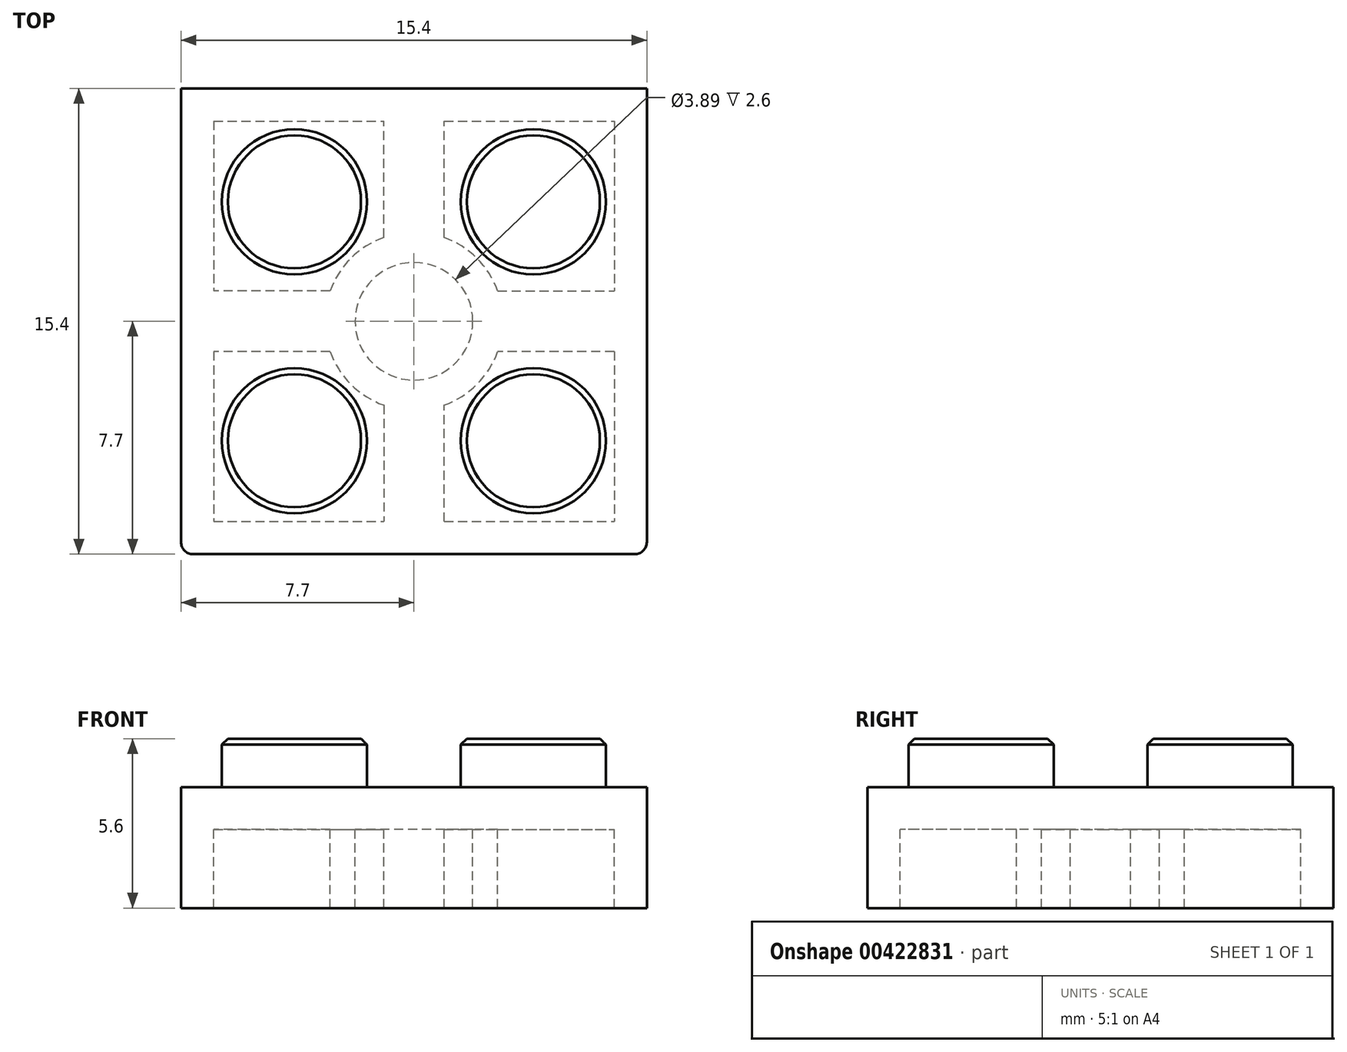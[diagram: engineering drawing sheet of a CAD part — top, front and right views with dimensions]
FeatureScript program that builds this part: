
annotation { "Feature Type Name" : "Feature", "Feature Type Description" : "" }
export const myFeature = defineFeature(function(context is Context, id is Id, definition is map)
    precondition{}
    {
        {
            var Q0;
            Q0=qCreatedBy(makeId("Top.planeOp"),FACE);
            var sketch = newSketch(context, id + "F0", { "sketchPlane" : qUnion([Q0])});
            skLineSegment(sketch, "E0.bottom", {"start": v(-7.7, 7.7) * mm, "end": v(7.7, 7.7) * mm});
            skLineSegment(sketch, "E0.top", {"start": v(-7.7, -7.7) * mm, "end": v(7.7, -7.7) * mm});
            skLineSegment(sketch, "E0.left", {"start": v(-7.7, 7.7) * mm, "end": v(-7.7, -7.7) * mm});
            skLineSegment(sketch, "E0.right", {"start": v(7.7, 7.7) * mm, "end": v(7.7, -7.7) * mm});
            skLineSegment(sketch, "E1", {"start": v(-7.7, 7.7) * mm, "end": v(7.7, -7.7) * mm, "construction": true});
            skLineSegment(sketch, "E2", {"start": v(7.7, 7.7) * mm, "end": v(-7.7, -7.7) * mm, "construction": true});
            skLineSegment(sketch, "E3.bottom", {"start": v(-3.95, 3.95) * mm, "end": v(3.95, 3.95) * mm, "construction": true});
            skLineSegment(sketch, "E3.top", {"start": v(-3.95, -3.95) * mm, "end": v(3.95, -3.95) * mm, "construction": true});
            skLineSegment(sketch, "E3.left", {"start": v(-3.95, 3.95) * mm, "end": v(-3.95, -3.95) * mm, "construction": true});
            skLineSegment(sketch, "E3.right", {"start": v(3.95, 3.95) * mm, "end": v(3.95, -3.95) * mm, "construction": true});
            skCircle(sketch, "E4", {"center": v(3.95, 3.95) * mm, "radius": 2.4 * mm});
            skCircle(sketch, "E5", {"center": v(-3.95, 3.95) * mm, "radius": 2.4 * mm});
            skCircle(sketch, "E6", {"center": v(-3.95, -3.95) * mm, "radius": 2.4 * mm});
            skCircle(sketch, "E7", {"center": v(3.95, -3.95) * mm, "radius": 2.4 * mm});
            skLineSegment(sketch, "E8.bottom", {"start": v(-6.35, 6.35) * mm, "end": v(6.35, 6.35) * mm});
            skLineSegment(sketch, "E8.top", {"start": v(-6.35, -6.35) * mm, "end": v(6.35, -6.35) * mm});
            skLineSegment(sketch, "E8.left", {"start": v(-6.35, 6.35) * mm, "end": v(-6.35, -6.35) * mm});
            skLineSegment(sketch, "E8.right", {"start": v(6.35, 6.35) * mm, "end": v(6.35, -6.35) * mm});
            skCircle(sketch, "E9", {"center": v(0, 0) * mm, "radius": 2.95 * mm});
            skCircle(sketch, "E10", {"center": v(0, 0) * mm, "radius": 1.95 * mm});
            skLineSegment(sketch, "E11.bottom", {"start": v(-6.62, 6.62) * mm, "end": v(6.62, 6.62) * mm});
            skLineSegment(sketch, "E11.top", {"start": v(-6.62, -6.62) * mm, "end": v(6.62, -6.62) * mm});
            skLineSegment(sketch, "E11.left", {"start": v(-6.62, 6.62) * mm, "end": v(-6.62, -6.62) * mm});
            skLineSegment(sketch, "E11.right", {"start": v(6.62, 6.62) * mm, "end": v(6.62, -6.62) * mm});
            skPoint(sketch, "E12.center.orphan", {"position": v(0, 7.7) * mm});
            skPoint(sketch, "E13.center.orphan", {"position": v(0, 11.7) * mm});
            skSolve(sketch);
        }
        {
            var Q0;
            Q0=makeQuery(id+"F0.imprint","IMPRINT",FACE,{"disambiguationData":[TD([[makeQuery(id+"F0.imprint","IMPRINT",EDGE,{"derivedFrom":sQuery(id+"F0.wireOp",EDGE,"E0.bottom")}),1.0]])]});
            var Q1;
            Q1=makeQuery(id+"F0.imprint","IMPRINT",FACE,{"disambiguationData":[TD([[makeQuery(id+"F0.imprint","IMPRINT",EDGE,{"derivedFrom":sQuery(id+"F0.wireOp",EDGE,"E4")}),1.0]])]});
            var Q2;
            Q2=makeQuery(id+"F0.imprint","IMPRINT",FACE,{"disambiguationData":[TD([[makeQuery(id+"F0.imprint","IMPRINT",EDGE,{"derivedFrom":sQuery(id+"F0.wireOp",EDGE,"E5")}),1.0]])]});
            var Q3;
            Q3=makeQuery(id+"F0.imprint","IMPRINT",FACE,{"disambiguationData":[TD([[makeQuery(id+"F0.imprint","IMPRINT",EDGE,{"derivedFrom":sQuery(id+"F0.wireOp",EDGE,"E6")}),1.0]])]});
            var Q4;
            Q4=makeQuery(id+"F0.imprint","IMPRINT",FACE,{"disambiguationData":[TD([[makeQuery(id+"F0.imprint","IMPRINT",EDGE,{"derivedFrom":sQuery(id+"F0.wireOp",EDGE,"E7")}),1.0]])]});
            var Q5;
            Q5=makeQuery(id+"F0.imprint","IMPRINT",FACE,{"disambiguationData":[TD([[makeQuery(id+"F0.imprint","IMPRINT",EDGE,{"derivedFrom":sQuery(id+"F0.wireOp",EDGE,"E0.bottom")}),-1.0]])]});
            var Q6;
            {var subQ5=sQuery(id+"F0.wireOp",EDGE,"E8.bottom");var subQ13=sQuery(id+"F0.wireOp",EDGE,"E4");var subQ14=makeQuery(id+"F0.imprint","INTERSECT",VERTEX,{"derivedFrom":[subQ13,subQ5]});Q6=makeQuery(id+"F0.imprint","IMPRINT",FACE,{"disambiguationData":[TD([[makeQuery(id+"F0.imprint","IMPRINT",EDGE,{"disambiguationData":[TD([[subQ14,-1.0]])],"derivedFrom":subQ13}),-1.0]])]});}
            var Q7;
            {var subQ0=sQuery(id+"F0.wireOp",EDGE,"E8.top");var subQ1=sQuery(id+"F0.wireOp",EDGE,"E6");var subQ2=makeQuery(id+"F0.imprint","INTERSECT",VERTEX,{"derivedFrom":[subQ1,subQ0]});Q7=makeQuery(id+"F0.imprint","IMPRINT",FACE,{"disambiguationData":[TD([[makeQuery(id+"F0.imprint","IMPRINT",EDGE,{"disambiguationData":[TD([[subQ2,1.0]])],"derivedFrom":subQ1}),-1.0]])]});}
            var Q8;
            {var subQ0=sQuery(id+"F0.wireOp",EDGE,"E8.bottom");var subQ1=sQuery(id+"F0.wireOp",EDGE,"E5");var subQ2=makeQuery(id+"F0.imprint","INTERSECT",VERTEX,{"derivedFrom":[subQ1,subQ0]});Q8=makeQuery(id+"F0.imprint","IMPRINT",FACE,{"disambiguationData":[TD([[makeQuery(id+"F0.imprint","IMPRINT",EDGE,{"disambiguationData":[TD([[subQ2,-1.0]])],"derivedFrom":subQ1}),-1.0]])]});}
            var Q9;
            {var subQ0=sQuery(id+"F0.wireOp",EDGE,"E8.bottom");var subQ1=sQuery(id+"F0.wireOp",EDGE,"E4");var subQ2=makeQuery(id+"F0.imprint","INTERSECT",VERTEX,{"derivedFrom":[subQ1,subQ0]});Q9=makeQuery(id+"F0.imprint","IMPRINT",FACE,{"disambiguationData":[TD([[makeQuery(id+"F0.imprint","IMPRINT",EDGE,{"disambiguationData":[TD([[subQ2,1.0]])],"derivedFrom":subQ1}),-1.0]])]});}
            var Q10;
            {var subQ0=sQuery(id+"F0.wireOp",EDGE,"E8.top");var subQ1=sQuery(id+"F0.wireOp",EDGE,"E7");var subQ2=makeQuery(id+"F0.imprint","INTERSECT",VERTEX,{"derivedFrom":[subQ1,subQ0]});Q10=makeQuery(id+"F0.imprint","IMPRINT",FACE,{"disambiguationData":[TD([[makeQuery(id+"F0.imprint","IMPRINT",EDGE,{"disambiguationData":[TD([[subQ2,-1.0]])],"derivedFrom":subQ1}),-1.0]])]});}
            var Q11;
            {var subQ0=sQuery(id+"F0.wireOp",EDGE,"E8.left");var subQ1=sQuery(id+"F0.wireOp",EDGE,"E5");var subQ2=makeQuery(id+"F0.imprint","INTERSECT",VERTEX,{"derivedFrom":[subQ1,subQ0]});Q11=makeQuery(id+"F0.imprint","IMPRINT",FACE,{"disambiguationData":[TD([[makeQuery(id+"F0.imprint","IMPRINT",EDGE,{"disambiguationData":[TD([[subQ2,-1.0]])],"derivedFrom":subQ1}),-1.0]])]});}
            var Q12;
            {var subQ0=sQuery(id+"F0.wireOp",EDGE,"E8.right");var subQ1=sQuery(id+"F0.wireOp",EDGE,"E4");var subQ2=makeQuery(id+"F0.imprint","INTERSECT",VERTEX,{"derivedFrom":[subQ1,subQ0]});Q12=makeQuery(id+"F0.imprint","IMPRINT",FACE,{"disambiguationData":[TD([[makeQuery(id+"F0.imprint","IMPRINT",EDGE,{"disambiguationData":[TD([[subQ2,1.0]])],"derivedFrom":subQ1}),-1.0]])]});}
            var Q13;
            {var subQ0=sQuery(id+"F0.wireOp",EDGE,"E9");var subQ1=sQuery(id+"F0.wireOp",EDGE,"E6");var subQ2=makeQuery(id+"F0.imprint","INTERSECT",VERTEX,{"derivedFrom":[subQ1,subQ0]});Q13=makeQuery(id+"F0.imprint","IMPRINT",FACE,{"disambiguationData":[TD([[makeQuery(id+"F0.imprint","IMPRINT",EDGE,{"disambiguationData":[TD([[subQ2,1.0]])],"derivedFrom":subQ1}),-1.0]])]});}
            var Q14;
            Q14=makeQuery(id+"F0.imprint","IMPRINT",FACE,{"disambiguationData":[TD([[makeQuery(id+"F0.imprint","IMPRINT",EDGE,{"derivedFrom":sQuery(id+"F0.wireOp",EDGE,"E10")}),-1.0]])]});
            var Q15;
            Q15=makeQuery(id+"F0.imprint","IMPRINT",FACE,{"disambiguationData":[TD([[makeQuery(id+"F0.imprint","IMPRINT",EDGE,{"derivedFrom":sQuery(id+"F0.wireOp",EDGE,"E10")}),1.0]])]});
            var Q16;
            Q16=makeQuery(id+"F0.imprint","IMPRINT",FACE,{"disambiguationData":[TD([[makeQuery(id+"F0.imprint","IMPRINT",EDGE,{"derivedFrom":sQuery(id+"F0.wireOp",EDGE,"E11.bottom")}),-1.0]])]});
            extrude(context, id + "F1", {"entities" : qUnion([Q0, Q1, Q2, Q3, Q4, Q5, Q6, Q7, Q8, Q9, Q10, Q11, Q12, Q13, Q14, Q15, Q16]), "oppositeDirection" : true, "depth" : 1.4 * mm});
        }
        {
            var Q0;
            Q0=makeQuery(id+"F0.imprint","IMPRINT",FACE,{"disambiguationData":[TD([[makeQuery(id+"F0.imprint","IMPRINT",EDGE,{"derivedFrom":sQuery(id+"F0.wireOp",EDGE,"E5")}),1.0]])]});
            var Q1;
            Q1=makeQuery(id+"F0.imprint","IMPRINT",FACE,{"disambiguationData":[TD([[makeQuery(id+"F0.imprint","IMPRINT",EDGE,{"derivedFrom":sQuery(id+"F0.wireOp",EDGE,"E4")}),1.0]])]});
            var Q2;
            Q2=makeQuery(id+"F0.imprint","IMPRINT",FACE,{"disambiguationData":[TD([[makeQuery(id+"F0.imprint","IMPRINT",EDGE,{"derivedFrom":sQuery(id+"F0.wireOp",EDGE,"E7")}),1.0]])]});
            var Q3;
            Q3=makeQuery(id+"F0.imprint","IMPRINT",FACE,{"disambiguationData":[TD([[makeQuery(id+"F0.imprint","IMPRINT",EDGE,{"derivedFrom":sQuery(id+"F0.wireOp",EDGE,"E6")}),1.0]])]});
            extrude(context, id + "F2", {"entities" : qUnion([Q0, Q1, Q2, Q3]), "operationType" : NewBodyOperationType.ADD, "depth" : 1.6 * mm});
        }
        {
            var Q0;
            Q0=makeQuery(id+"F0.imprint","IMPRINT",FACE,{"disambiguationData":[TD([[makeQuery(id+"F0.imprint","IMPRINT",EDGE,{"derivedFrom":sQuery(id+"F0.wireOp",EDGE,"E10")}),-1.0]])]});
            var Q1;
            Q1=makeQuery(id+"F0.imprint","IMPRINT",FACE,{"disambiguationData":[TD([[makeQuery(id+"F0.imprint","IMPRINT",EDGE,{"derivedFrom":sQuery(id+"F0.wireOp",EDGE,"E0.bottom")}),-1.0]])]});
            var Q2;
            Q2=makeQuery(id+"F0.imprint","IMPRINT",FACE,{"disambiguationData":[TD([[makeQuery(id+"F0.imprint","IMPRINT",EDGE,{"derivedFrom":sQuery(id+"F0.wireOp",EDGE,"E0.bottom")}),1.0]])]});
            extrude(context, id + "F3", {"entities" : qUnion([Q0, Q1, Q2]), "operationType" : NewBodyOperationType.ADD, "oppositeDirection" : true, "depth" : 4 * mm});
        }
        {
            var Q0;
            {var subQ0=sQuery(id+"F0.wireOp",EDGE,"E0.right");var subQ1=sQuery(id+"F0.wireOp",EDGE,"E0.top");Q0=makeQuery(id+"F3.boolean.opBoolean","MERGE",EDGE,{"derivedFrom":[makeQuery(id+"F1.opExtrude","SWEPT_EDGE",EDGE,{"disambiguationData":[OSD([subQ1,subQ0])]}),makeQuery(id+"F3.opExtrude","SWEPT_EDGE",EDGE,{"disambiguationData":[OSD([subQ1,subQ0])]})]});}
            var Q1;
            {var subQ0=sQuery(id+"F0.wireOp",EDGE,"E0.left");var subQ1=sQuery(id+"F0.wireOp",EDGE,"E0.top");Q1=makeQuery(id+"F3.boolean.opBoolean","MERGE",EDGE,{"derivedFrom":[makeQuery(id+"F1.opExtrude","SWEPT_EDGE",EDGE,{"disambiguationData":[OSD([subQ1,subQ0])]}),makeQuery(id+"F3.opExtrude","SWEPT_EDGE",EDGE,{"disambiguationData":[OSD([subQ1,subQ0])]})]});}
            fillet(context, id + "F4", {"entities" : qUnion([Q0, Q1]), "radius" : 0.4 * mm, "tangentPropagation" : true, "allowEdgeOverflow" : false});
        }
        {
            var Q0;
            Q0=makeQuery(id+"F3.boolean.opBoolean","SPLIT",FACE,{"disambiguationData":[TD([makeQuery(id+"F3.opExtrude","SWEPT_FACE",FACE,{"disambiguationData":[OSD([sQuery(id+"F0.wireOp",EDGE,"E9")])]})])],"derivedFrom":makeQuery(id+"F1.opExtrude","CAP_FACE",FACE,{"disambiguationData":[OSD([sQuery(id+"F0.wireOp",EDGE,"E0.top"),sQuery(id+"F0.wireOp",EDGE,"E0.left"),sQuery(id+"F0.wireOp",EDGE,"E0.right"),sQuery(id+"F0.wireOp",EDGE,"E12"),sQuery(id+"F0.wireOp",EDGE,"E13")])],"isStart":false})});
            var sketch = newSketch(context, id + "F5", { "sketchPlane" : qUnion([Q0])});
            skLineSegment(sketch, "E14.bottom", {"start": v(-1, 2.77) * mm, "end": v(1, 2.77) * mm});
            skLineSegment(sketch, "E14.top", {"start": v(-1, 6.62) * mm, "end": v(1, 6.62) * mm});
            skLineSegment(sketch, "E14.left", {"start": v(-1, 2.77) * mm, "end": v(-1, 6.62) * mm});
            skLineSegment(sketch, "E14.right", {"start": v(1, 2.77) * mm, "end": v(1, 6.62) * mm});
            skLineSegment(sketch, "E15.bottom", {"start": v(2.77, 1) * mm, "end": v(6.62, 1) * mm});
            skLineSegment(sketch, "E15.top", {"start": v(2.77, -1) * mm, "end": v(6.62, -1) * mm});
            skLineSegment(sketch, "E15.left", {"start": v(2.77, 1) * mm, "end": v(2.77, -1) * mm});
            skLineSegment(sketch, "E15.right", {"start": v(6.62, 1) * mm, "end": v(6.62, -1) * mm});
            skLineSegment(sketch, "E16.bottom", {"start": v(1, -2.77) * mm, "end": v(-1, -2.77) * mm});
            skLineSegment(sketch, "E16.top", {"start": v(1, -6.62) * mm, "end": v(-1, -6.62) * mm});
            skLineSegment(sketch, "E16.left", {"start": v(1, -2.77) * mm, "end": v(1, -6.62) * mm});
            skLineSegment(sketch, "E16.right", {"start": v(-1, -2.77) * mm, "end": v(-1, -6.62) * mm});
            skLineSegment(sketch, "E17.bottom", {"start": v(-2.77, -1) * mm, "end": v(-6.62, -1) * mm});
            skLineSegment(sketch, "E17.top", {"start": v(-2.77, 1) * mm, "end": v(-6.62, 1) * mm});
            skLineSegment(sketch, "E17.left", {"start": v(-2.77, -1) * mm, "end": v(-2.77, 1) * mm});
            skLineSegment(sketch, "E17.right", {"start": v(-6.62, -1) * mm, "end": v(-6.62, 1) * mm});
            skSolve(sketch);
        }
        {
            var Q0;
            {var subQ0=sQuery(id+"F5.wireOp",EDGE,"E17.bottom");Q0=makeQuery(id+"F5.imprint","IMPRINT",FACE,{"disambiguationData":[TD([[makeQuery(id+"F5.imprint","IMPRINT",EDGE,{"derivedFrom":subQ0}),-1.0]])]});}
            var Q1;
            Q1=makeQuery(id+"F5.imprint","IMPRINT",FACE,{"disambiguationData":[TD([[makeQuery(id+"F5.imprint","IMPRINT",EDGE,{"derivedFrom":sQuery(id+"F5.wireOp",EDGE,"E14.top")}),-1.0]])]});
            var Q2;
            {var subQ0=sQuery(id+"F5.wireOp",EDGE,"E15.bottom");Q2=makeQuery(id+"F5.imprint","IMPRINT",FACE,{"disambiguationData":[TD([[makeQuery(id+"F5.imprint","IMPRINT",EDGE,{"derivedFrom":subQ0}),-1.0]])]});}
            var Q3;
            Q3=makeQuery(id+"F5.imprint","IMPRINT",FACE,{"disambiguationData":[TD([[makeQuery(id+"F5.imprint","IMPRINT",EDGE,{"derivedFrom":sQuery(id+"F5.wireOp",EDGE,"E16.top")}),1.0]])]});
            var Q4;
            Q4=makeQuery(id+"F3.opExtrude","CAP_FACE",FACE,{"disambiguationData":[OSD([sQuery(id+"F0.wireOp",EDGE,"E9"),sQuery(id+"F0.wireOp",EDGE,"E10")])],"isStart":false});
            extrude(context, id + "F6", {"entities" : qUnion([Q0, Q1, Q2, Q3]), "operationType" : NewBodyOperationType.ADD, "endBound" : BoundingType.UP_TO_SURFACE, "endBoundEntityFace" : qUnion([Q4]), "depth" : 25 * mm});
        }
        {
            var Q0;
            Q0=makeQuery(id+"F2.opExtrude","CAP_FACE",FACE,{"disambiguationData":[OSD([sQuery(id+"F0.wireOp",EDGE,"E6")])],"isStart":false});
            var Q1;
            Q1=makeQuery(id+"F2.opExtrude","CAP_FACE",FACE,{"disambiguationData":[OSD([sQuery(id+"F0.wireOp",EDGE,"E5")])],"isStart":false});
            var Q2;
            Q2=makeQuery(id+"F2.opExtrude","CAP_EDGE",EDGE,{"disambiguationData":[OSD([sQuery(id+"F0.wireOp",EDGE,"E4")])],"isStart":false});
            var Q3;
            Q3=makeQuery(id+"F2.opExtrude","CAP_FACE",FACE,{"disambiguationData":[OSD([sQuery(id+"F0.wireOp",EDGE,"E7")])],"isStart":false});
            chamfer(context, id + "F7", {"entities" : qUnion([Q0, Q1, Q2, Q3]), "width" : 0.2 * mm, "tangentPropagation" : true});
        }
    });
